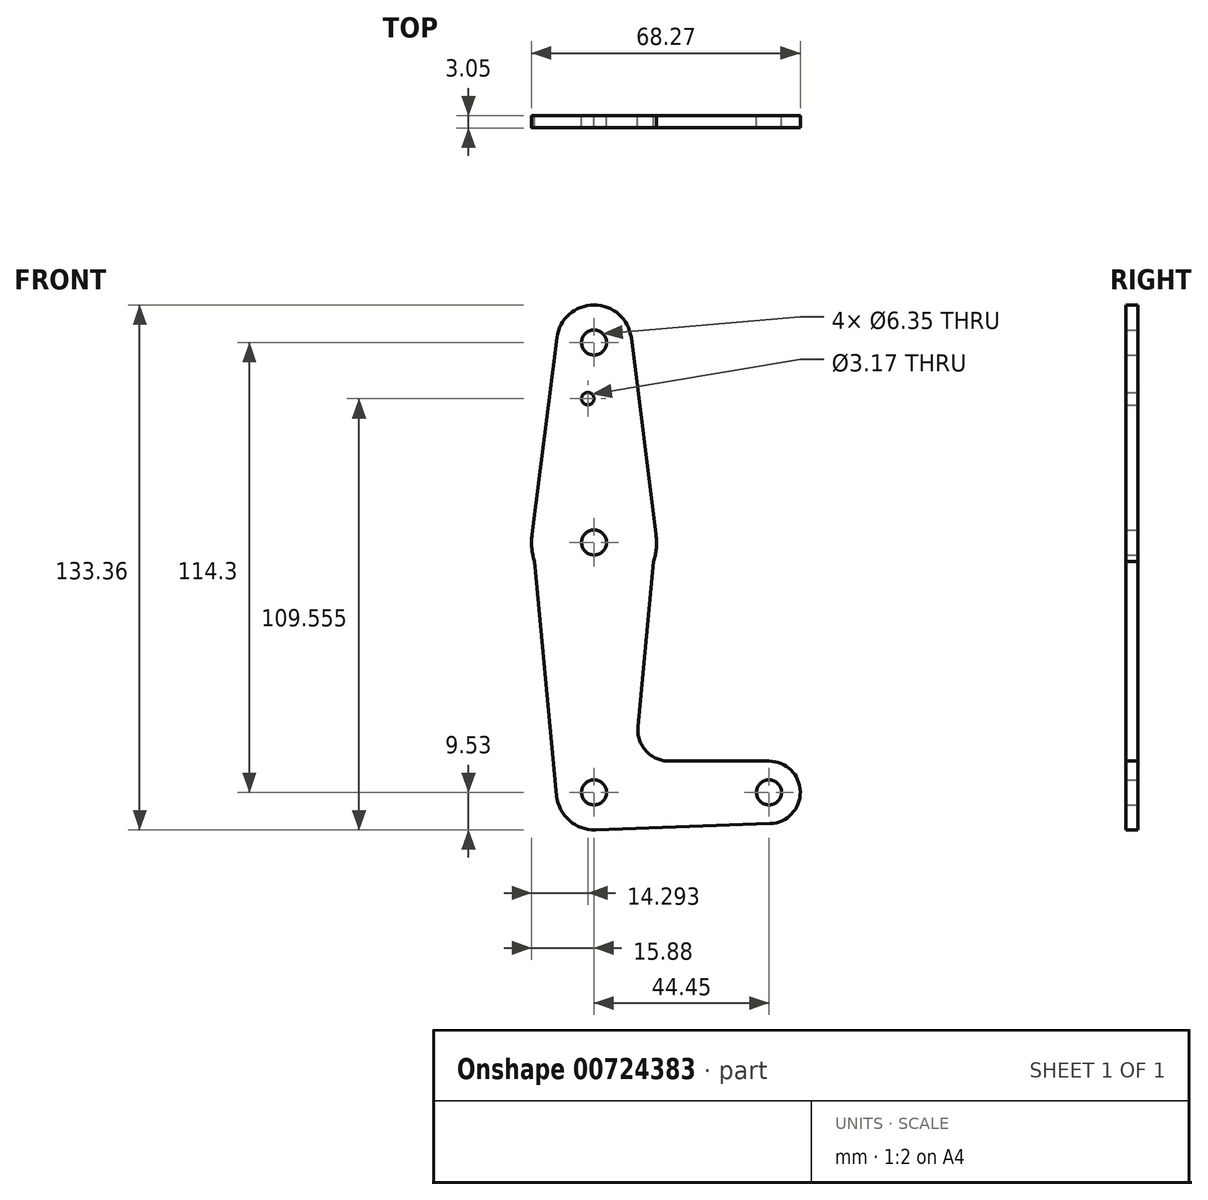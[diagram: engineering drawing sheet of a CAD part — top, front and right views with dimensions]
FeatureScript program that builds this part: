
annotation { "Feature Type Name" : "Feature", "Feature Type Description" : "" }
export const myFeature = defineFeature(function(context is Context, id is Id, definition is map)
    precondition{}
    {
        {
            var Q0;
            Q0=qCreatedBy(makeId("Front.planeOp"),FACE);
            var sketch = newSketch(context, id + "F0", { "sketchPlane" : qUnion([Q0])});
            skLineSegment(sketch, "E0", {"start": v(0, 0) * mm, "end": v(0, 114.3) * mm, "construction": true});
            skLineSegment(sketch, "E1", {"start": v(0, 0) * mm, "end": v(44.45, 0) * mm, "construction": true});
            skCircle(sketch, "E2", {"center": v(0, 114.3) * mm, "radius": 9.53 * mm});
            skCircle(sketch, "E3", {"center": v(0, 0) * mm, "radius": 9.53 * mm});
            skCircle(sketch, "E4", {"center": v(0, 63.5) * mm, "radius": 15.88 * mm});
            skCircle(sketch, "E5", {"center": v(44.45, 0) * mm, "radius": 7.94 * mm});
            skLineSegment(sketch, "E6", {"start": v(-9.45, 115.5) * mm, "end": v(-15.75, 65.48) * mm});
            skLineSegment(sketch, "E7", {"start": v(-15.75, 65.48) * mm, "end": v(-9.48, -0.9) * mm});
            skLineSegment(sketch, "E8", {"start": v(9.45, 115.5) * mm, "end": v(15.75, 65.48) * mm});
            skLineSegment(sketch, "E9", {"start": v(15.75, 65.48) * mm, "end": v(11.14, 16.64) * mm});
            skLineSegment(sketch, "E10", {"start": v(19.05, 7.94) * mm, "end": v(44.45, 7.94) * mm});
            skLineSegment(sketch, "E11", {"start": v(0.34, -9.52) * mm, "end": v(44.73, -7.93) * mm});
            skCircle(sketch, "E12", {"center": v(0, 114.3) * mm, "radius": 3.18 * mm});
            skCircle(sketch, "E13", {"center": v(0, 0) * mm, "radius": 3.18 * mm});
            skCircle(sketch, "E14", {"center": v(0, 63.5) * mm, "radius": 3.18 * mm});
            skCircle(sketch, "E15", {"center": v(44.45, 0) * mm, "radius": 3.18 * mm});
            skCircle(sketch, "E16", {"center": v(-1.59, 100.03) * mm, "radius": 1.59 * mm});
            skArc(sketch, "E17.filletArc", {"start": v(11.14, 16.64) * mm, "mid": v(13.17, 10.54) * mm, "end": v(19.05, 7.94) * mm});
            skSolve(sketch);
        }
        {
            var Q0;
            Q0 = qSketchRegion(id + "F0", true);
            extrude(context, id + "F1", {"entities" : qUnion([Q0]), "depth" : 3.05 * mm, "offsetDistance" : 25.4 * mm});
        }
    });
